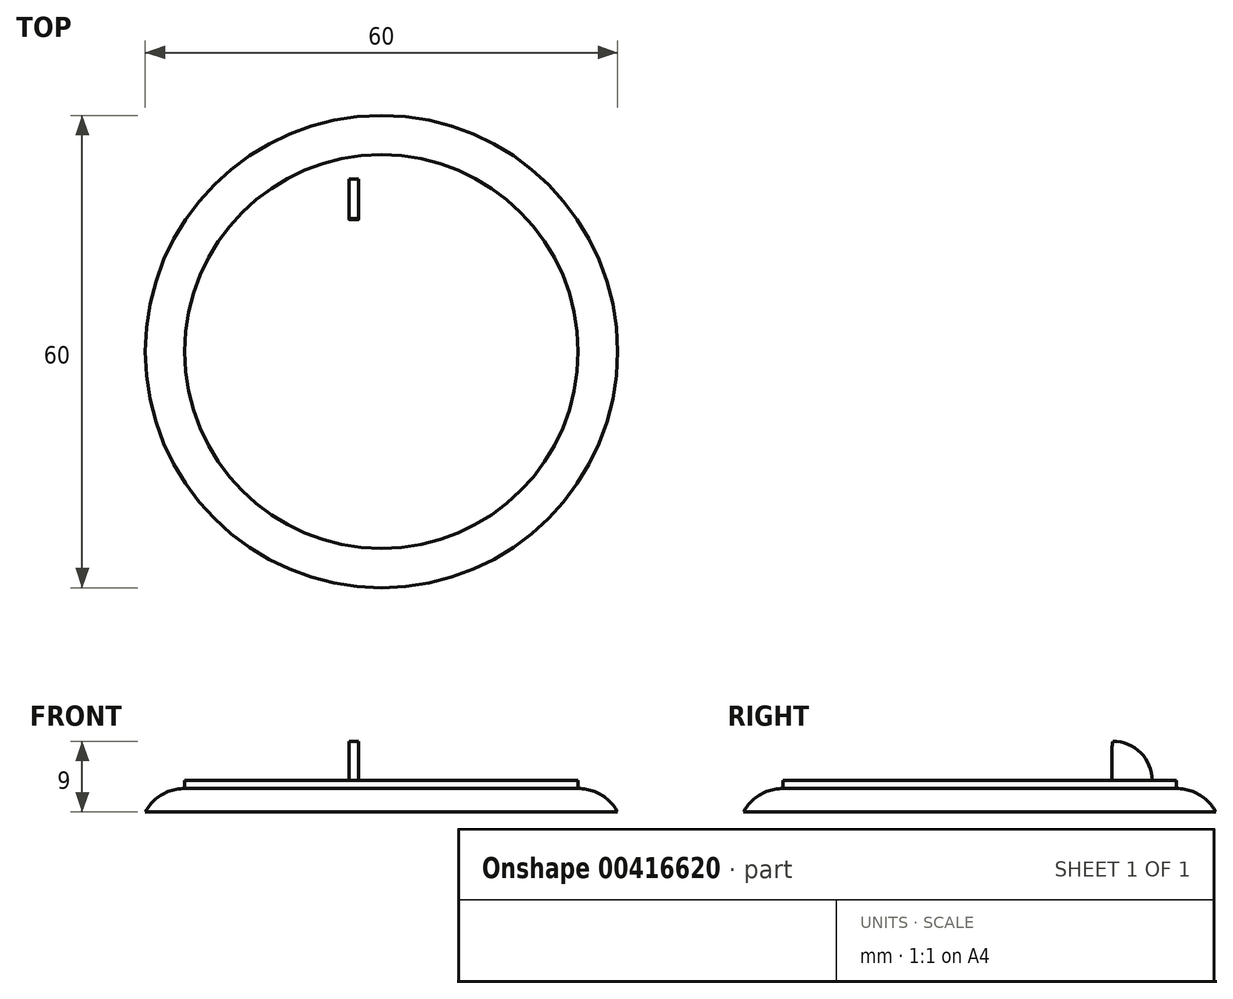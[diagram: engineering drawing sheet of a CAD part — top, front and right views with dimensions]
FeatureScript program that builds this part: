
annotation { "Feature Type Name" : "Feature", "Feature Type Description" : "" }
export const myFeature = defineFeature(function(context is Context, id is Id, definition is map)
    precondition{}
    {
        {
            var Q0;
            Q0=qCreatedBy(makeId("Front.planeOp"),FACE);
            var sketch = newSketch(context, id + "F0", { "sketchPlane" : qUnion([Q0])});
            skLineSegment(sketch, "E0", {"start": v(0, 0) * mm, "end": v(-30, 0) * mm});
            skLineSegment(sketch, "E1", {"start": v(0, 0) * mm, "end": v(0, 3) * mm});
            skLineSegment(sketch, "E2", {"start": v(-25, 3) * mm, "end": v(0, 3) * mm});
            skArc(sketch, "E3", {"start": v(-25, 3) * mm, "mid": v(-27.92, 2.2) * mm, "end": v(-30, 0) * mm});
            skSolve(sketch);
        }
        {
            var Q0;
            Q0=makeQuery(id+"F0.imprint","IMPRINT",FACE,{"disambiguationData":[TD([[makeQuery(id+"F0.imprint","IMPRINT",EDGE,{"derivedFrom":sQuery(id+"F0.wireOp",EDGE,"E0")}),-1.0]])]});
            var Q1;
            Q1=sQuery(id+"F0.wireOp",EDGE,"E1");
            revolve(context, id + "F1", {"entities" : qUnion([Q0]), "axis" : qUnion([Q1]), "revolveType" : RevolveType.FULL});
        }
        {
            var Q0;
            Q0=makeQuery(id+"F1.opRevolve","SWEPT_FACE",FACE,{"disambiguationData":[OSD([sQuery(id+"F0.wireOp",EDGE,"E2")])]});
            var sketch = newSketch(context, id + "F2", { "sketchPlane" : qUnion([Q0])});
            skSolve(sketch);
        }
        {
            var Q0;
            Q0=makeQuery(id+"F1.opRevolve","SWEPT_FACE",FACE,{"disambiguationData":[OSD([sQuery(id+"F0.wireOp",EDGE,"E2")])]});
            var sketch = newSketch(context, id + "F3", { "sketchPlane" : qUnion([Q0])});
            skCircle(sketch, "E4", {"center": v(0, 0) * mm, "radius": 25 * mm});
            skSolve(sketch);
        }
        {
            var Q0;
            Q0 = qSketchRegion(id + "F2", true);
            var Q1;
            Q1=makeQuery(id+"F3.imprint","IMPRINT",FACE,{"disambiguationData":[TD([[makeQuery(id+"F3.imprint","IMPRINT",EDGE,{"derivedFrom":sQuery(id+"F3.wireOp",EDGE,"E4")}),-1.0]])]});
            extrude(context, id + "F4", {"entities" : qUnion([Q0, Q1]), "operationType" : NewBodyOperationType.ADD, "depth" : 1 * mm});
        }
        {
            var Q0;
            Q0=makeQuery(id+"F4.opExtrude","CAP_FACE",FACE,{"disambiguationData":[OSD([sQuery(id+"F3.wireOp",EDGE,"E4")])],"isStart":false});
            var sketch = newSketch(context, id + "F5", { "sketchPlane" : qUnion([Q0])});
            skLineSegment(sketch, "E5.bottom", {"start": v(-4.1, 21.9) * mm, "end": v(-2.92, 21.9) * mm});
            skLineSegment(sketch, "E5.top", {"start": v(-4.1, 16.76) * mm, "end": v(-2.92, 16.76) * mm});
            skLineSegment(sketch, "E5.left", {"start": v(-4.1, 21.9) * mm, "end": v(-4.1, 16.76) * mm});
            skLineSegment(sketch, "E5.right", {"start": v(-2.92, 21.9) * mm, "end": v(-2.92, 16.76) * mm});
            skSolve(sketch);
        }
        {
            var Q0;
            Q0=makeQuery(id+"F5.imprint","IMPRINT",FACE,{"disambiguationData":[TD([[makeQuery(id+"F5.imprint","IMPRINT",EDGE,{"derivedFrom":sQuery(id+"F5.wireOp",EDGE,"E5.bottom")}),-1.0]])]});
            extrude(context, id + "F6", {"entities" : qUnion([Q0]), "operationType" : NewBodyOperationType.ADD, "depth" : 5 * mm});
        }
        {
            var Q0;
            Q0=makeQuery(id+"F6.opExtrude","CAP_EDGE",EDGE,{"disambiguationData":[OSD([sQuery(id+"F5.wireOp",EDGE,"E5.bottom")])],"isStart":false});
            fillet(context, id + "F7", {"entities" : qUnion([Q0]), "radius" : 5 * mm, "allowEdgeOverflow" : false});
        }
        {
            var Q0;
            Q0=makeQuery(id+"F6.opExtrude","CAP_EDGE",EDGE,{"disambiguationData":[OSD([sQuery(id+"F5.wireOp",EDGE,"E5.top")])],"isStart":false});
            fillet(context, id + "F8", {"entities" : qUnion([Q0]), "radius" : 10 * mm, "tangentPropagation" : true, "allowEdgeOverflow" : false});
        }
    });
